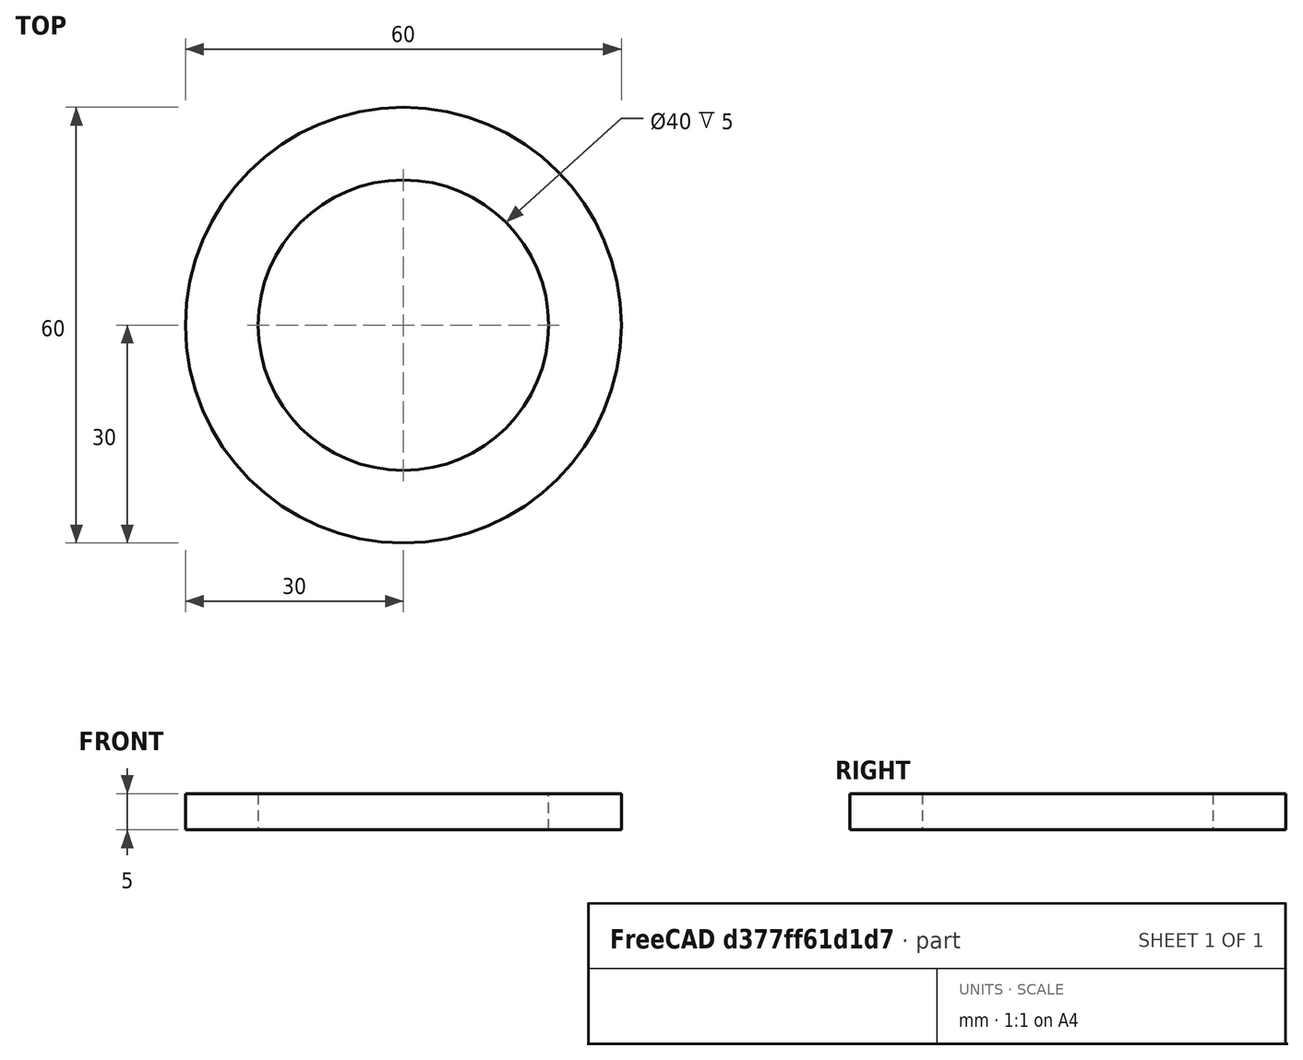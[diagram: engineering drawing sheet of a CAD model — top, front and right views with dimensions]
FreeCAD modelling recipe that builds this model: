
FCSTD DOCUMENT  (FreeCAD 0.19R24276 (Git))
Label: THRUST-40-60
License: All rights reserved
LicenseURL: http://en.wikipedia.org/wiki/All_rights_reserved
objects: Sketcher::SketchObject×1, PartDesign::Pad×1, PartDesign::CoordinateSystem×1, PartDesign::Body×1
note: 5 computed .brp shape members not serialized (recipe doc carries the construction recipe); baked Part::Feature solids carry a one-line shape summary decoded from their .brp

FEATURE [Sketcher::SketchObject] Sketch008
  FullyConstrained = false
  MapMode = 5
  Support = -> [XY_Plane006]
  sketch-geometry (2):
    g0: Circle CenterX=0 CenterY=0 CenterZ=0 NormalX=0 NormalY=0 NormalZ=1 AngleXU=0 Radius=20
    g1: Circle CenterX=0 CenterY=0 CenterZ=0 NormalX=0 NormalY=0 NormalZ=1 AngleXU=0 Radius=30
  constraints (4):
    c: Coincident(g0,g-1)
    c: Coincident(g0,g1)
    c: Diameter(g1) = 60
    c: Diameter(g0) = 40
FEATURE [PartDesign::Pad] Pad007
  AllowMultiFace = false
  Direction = (1,1,1)
  Length = 5
  Length2 = 100
  Profile = -> Sketch008
  Type = 0
FEATURE [PartDesign::CoordinateSystem] LCS_1
  AttacherType = Attacher::AttachEngine3D
  MapMode = 11
  Placement = pos=(0,0,0) rot=(0,0,1;1.5708rad)
  Support = -> [Pad007]
FEATURE [PartDesign::Body] Body002
  Group = -> [Sketch008,Pad007,LCS_1]
  Origin = -> Origin006
  Tip = -> Pad007
